# Revit family: Shower_Slide_Bar_Kit-GROHE-SmartActive-26547
name_source: partatom
category: Plumbing Fixtures
units: mm (PartAtom-declared; Revit-internal decimal feet)

## family parameters
Cut with Voids When Loaded = Yes
Host = Face
OmniClass Number = 23.40.20.21.47
OmniClass Title = Bath Grab Bars
Part Type = Normal
Room Calculation Point = No
Round Connector Dimension = Use Diameter
Shared = Yes

## types (2) — shared parameters
Assembly Code = D2010710
CW Connection = Yes
CWFU = 1.75
Connection Diameter = 1/2"
Default Elevation = 0"
Description = 24in. Shower Slide Bar Rainshower SmartActive
Flow Rate = 1.75 gpm (6.6 l/min)
HW Connection = Yes
HWFU = 1.75
Height = 96"
Installation Instruction Link = https://americanstandard.box.com
Installation Type = Wall Mounted
Length = 5 1/2"
Manufacturer = Grohe
Price = Prices may vary. Please consult Manufacturer Representative for most up-to-date price list.
Product Documentation Link = https://americanstandard.box.com
Product Page URL = https://www.grohe.us
Revised Date = 02/22/2022
Shower Height = 24 13/16"
URL = https://www.grohe.us
Vent Connection = No
Warranty Documentation Link = https://cdn.cloud.grohe.com
Waste Connection = No
Width = 5 1/2"
zero-valued in all types: WFU

## per-type parameters (varying)
| type | Finish | Material |
| 26547000 | Metal-GROHE-000-Starlight Chrome | Metal-Grohe-000-StarLight Chrome |
| 26547EN0 | Metal-Grohe-EN0-BrushedNickelInfinityFinish | Metal-Grohe-EN0-BrushedNickelInfinityFinish |

note: column(s) folded — value = type name in every type: Model

## geometry (parser evidence)
native form markers: Sweep x2
no freeform markers — native parametric forms only
